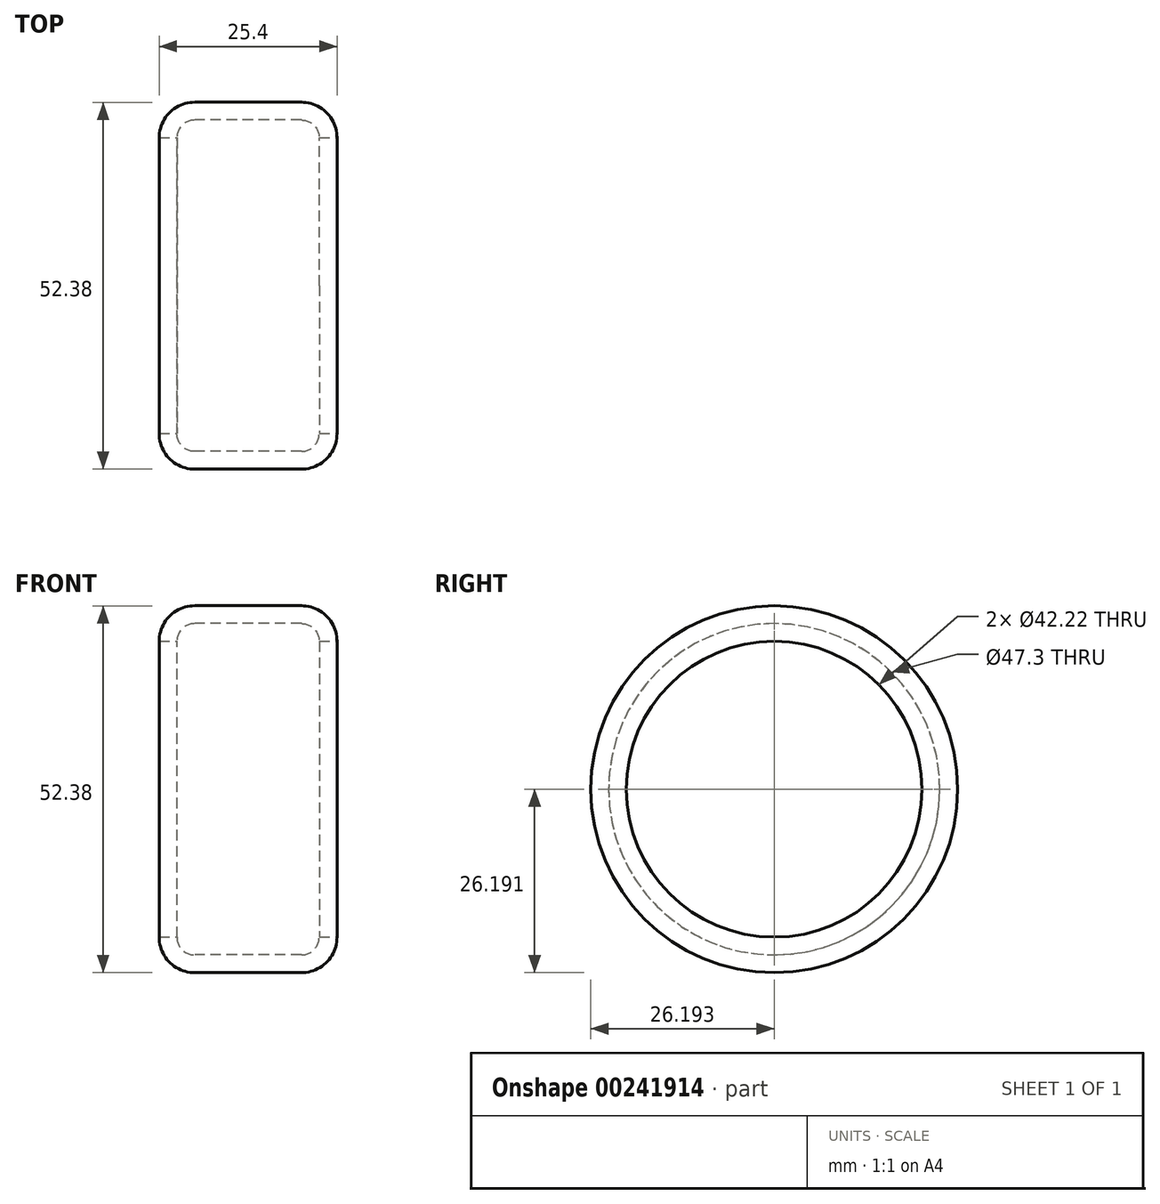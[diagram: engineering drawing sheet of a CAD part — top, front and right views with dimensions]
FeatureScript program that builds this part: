
annotation { "Feature Type Name" : "Feature", "Feature Type Description" : "" }
export const myFeature = defineFeature(function(context is Context, id is Id, definition is map)
    precondition{}
    {
        {
            var Q0;
            Q0=qCreatedBy(makeId("Right.planeOp"),FACE);
            var sketch = newSketch(context, id + "F0", { "sketchPlane" : qUnion([Q0])});
            skCircle(sketch, "E0", {"center": v(-9.93, 26.37) * mm, "radius": 26.19 * mm});
            skCircle(sketch, "E1", {"center": v(128.46, -46.87) * mm, "radius": 24.14 * mm});
            skSolve(sketch);
        }
        {
            var Q0;
            Q0=makeQuery(id+"F0.imprint","IMPRINT",FACE,{"disambiguationData":[TD([[makeQuery(id+"F0.imprint","IMPRINT",EDGE,{"derivedFrom":sQuery(id+"F0.wireOp",EDGE,"E0")}),1.0]])]});
            extrude(context, id + "F1", {"entities" : qUnion([Q0]), "depth" : 25.4 * mm});
        }
        {
            var Q0;
            Q0=makeQuery(id+"F1.opExtrude","CAP_FACE",FACE,{"disambiguationData":[OSD([sQuery(id+"F0.wireOp",EDGE,"E0")])],"isStart":false});
            var Q1;
            Q1=makeQuery(id+"F1.opExtrude","CAP_FACE",FACE,{"disambiguationData":[OSD([sQuery(id+"F0.wireOp",EDGE,"E0")])],"isStart":true});
            var Q2;
            Q2=makeQuery(id+"F1.opExtrude","CAP_EDGE",EDGE,{"disambiguationData":[OSD([sQuery(id+"F0.wireOp",EDGE,"E0")])],"isStart":false});
            var Q3;
            Q3=makeQuery(id+"F1.opExtrude","SWEPT_FACE",FACE,{"disambiguationData":[OSD([sQuery(id+"F0.wireOp",EDGE,"E0")])]});
            fillet(context, id + "F2", {"entities" : qUnion([Q0, Q1, Q2, Q3]), "radius" : 5.08 * mm, "tangentPropagation" : true, "allowEdgeOverflow" : false});
        }
        {
            var Q0;
            Q0=makeQuery(id+"F1.opExtrude","CAP_FACE",FACE,{"disambiguationData":[OSD([sQuery(id+"F0.wireOp",EDGE,"E0")])],"isStart":false});
            var Q1;
            Q1=makeQuery(id+"F1.opExtrude","CAP_FACE",FACE,{"disambiguationData":[OSD([sQuery(id+"F0.wireOp",EDGE,"E0")])],"isStart":true});
            shell(context, id + "F3", {"entities" : qUnion([Q0, Q1]), "thickness" : 2.54 * mm});
        }
    });
